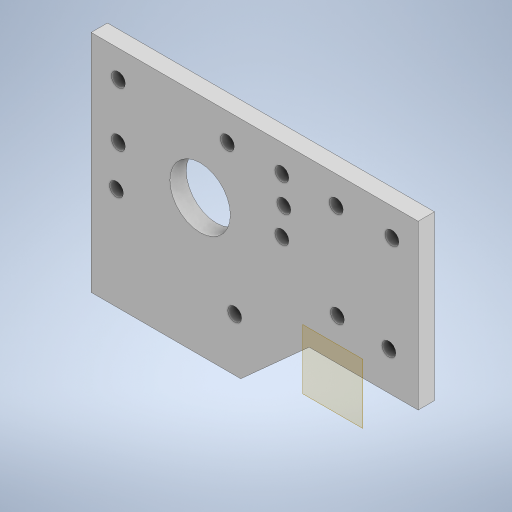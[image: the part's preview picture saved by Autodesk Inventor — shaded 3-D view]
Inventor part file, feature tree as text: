
AUTODESK INVENTOR PART (.ipt)
format: ipt  version: 2023.2 (Build 272271000, 271)  size: 604,672 bytes
history: native  units: mm
features: reference x13, other x4, sketch x3, hole x3, extrude x1, plane x1
ambient origin geometry x8: Origin, YZ Plane, XZ Plane, XY Plane, X Axis, Y Axis, Z Axis, Center Point
bodies: Body1 (feature_tree)
feature tree (25):
  sketch  "Sketch1"  dims[d0=120.0mm d1=40.0mm]
  extrude  "Extrusion2"  Depth=120.0mm
  plane  "Work Plane1"
  hole  "Hole2"  [1 undecoded]
  hole  "Hole3"  [1 undecoded]
  hole  "Hole4"  [1 undecoded]
  reference  "Reference1"
  reference  "Reference2"
  reference  "Reference3"
  reference  "Reference4"
  reference  "Reference5"
  reference  "Reference6"
  reference  "Reference7"
  reference  "Reference8"
  reference  "Reference9"
  reference  "Reference10"
  reference  "Reference11"
  reference  "Reference12"
  sketch  "Sketch2"  dims[d5=20.0mm d36=22.2mm]
  reference  "Reference13"
  sketch  "Sketch3"  dims[d37=32.5mm d41=47.0mm d42=47.0mm d43=9.2mm d44=9.2mm d45=15.0mm d47=50.0mm d48=50.0mm d49=6.0mm d50=0.0mm d58=5.1mm d59=6.0mm d60=9.2mm d61=3.0mm d62=90.0deg d63=8.0mm d64=20.594885mm d65=5.1mm d66=6.0mm d67=9.2mm d68=3.0mm d69=90.0deg d70=8.0mm d71=20.594885mm d72=5.1mm d73=6.0mm d74=9.2mm d75=3.0mm d76=90.0deg d77=8.0mm d78=20.594885mm d79=15.0mm]
  parser-record x1  (decoder bookkeeping rows leaked as tree rows — omitted from the tree; the rows remain in map.json)
  other  "Main Assembly.iam"
  other  "C beam extrusion 250:1"
  other  "Y axis motor mount:1"
note: 3 required parameter values undecoded (feature->parameter linkage not recoverable at this tier; creation-order binding heuristic only, values carry confidence <= 0.55)
note: 1 file-system path scrubbed to <path> (originals preserved in map.json)
